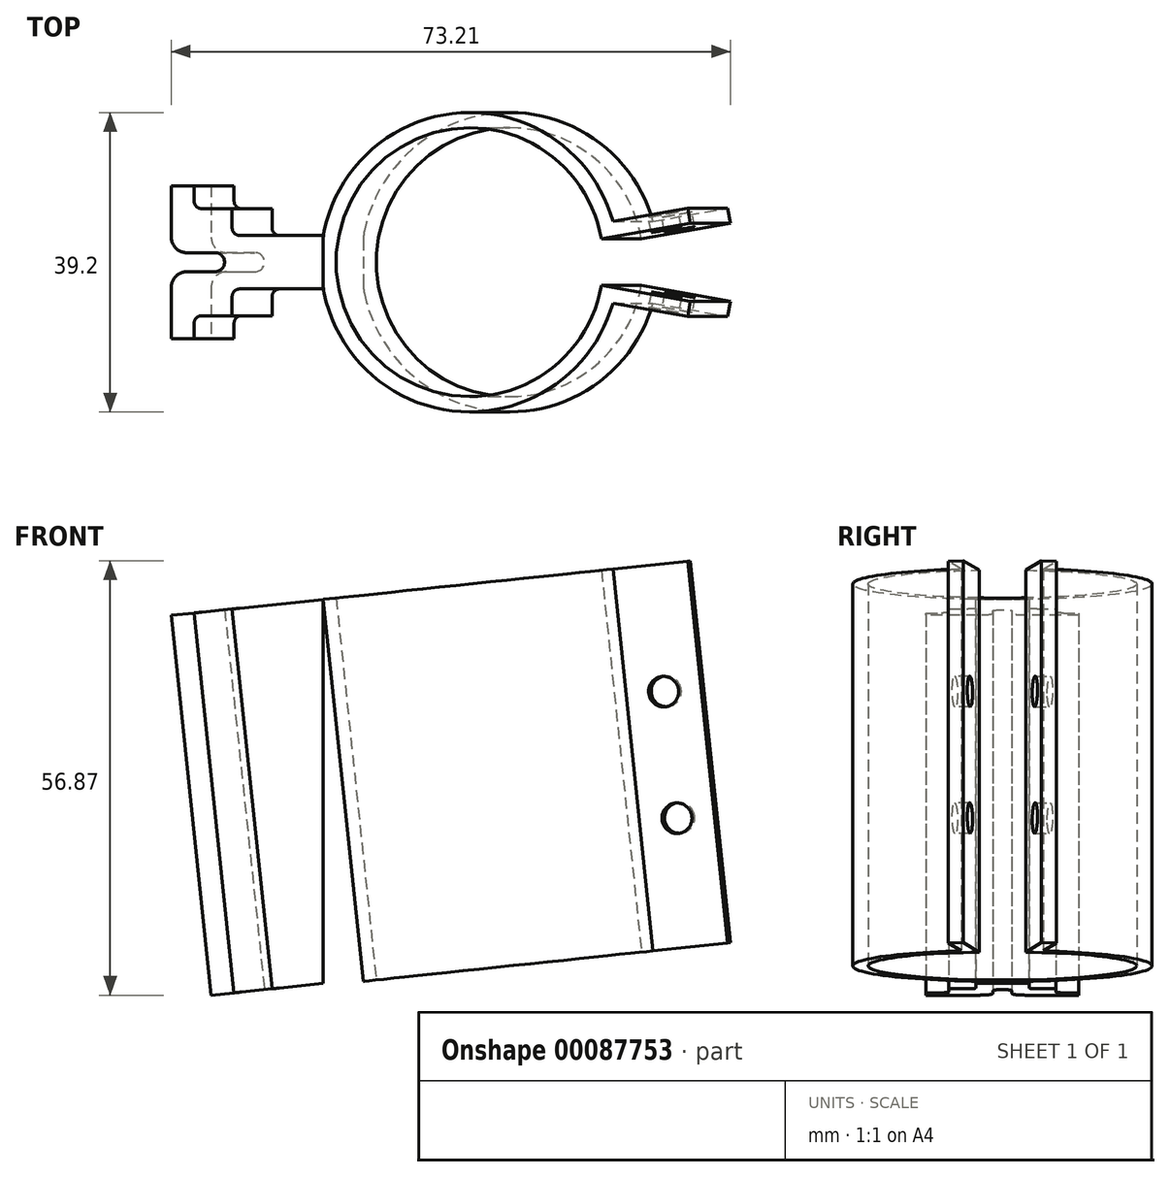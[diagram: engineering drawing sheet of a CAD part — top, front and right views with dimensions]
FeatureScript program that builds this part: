
annotation { "Feature Type Name" : "Feature", "Feature Type Description" : "" }
export const myFeature = defineFeature(function(context is Context, id is Id, definition is map)
    precondition{}
    {
        {
            var Q0;
            Q0=qCreatedBy(makeId("Top.planeOp"),FACE);
            var sketch = newSketch(context, id + "F0", { "sketchPlane" : qUnion([Q0])});
            skCircle(sketch, "E0", {"center": v(0, 0) * mm, "radius": 17.6 * mm});
            skCircle(sketch, "E1", {"center": v(0, 0) * mm, "radius": 19.6 * mm});
            skLineSegment(sketch, "E2", {"start": v(0, 0) * mm, "end": v(44.07, 0) * mm});
            skLineSegment(sketch, "E3", {"start": v(44.07, 0) * mm, "end": v(44.07, 7.77) * mm, "construction": true});
            skLineSegment(sketch, "E4", {"start": v(44.07, 7.77) * mm, "end": v(0, 0) * mm});
            skLineSegment(sketch, "E5.MirrorCS", {"start": v(44.07, -7.77) * mm, "end": v(0, 0) * mm});
            skLineSegment(sketch, "E6", {"start": v(18.85, 5.35) * mm, "end": v(28.7, 7.1) * mm});
            skLineSegment(sketch, "E7", {"start": v(28.7, 7.1) * mm, "end": v(29.05, 5.12) * mm});
            skLineSegment(sketch, "E8", {"start": v(-19.28, 3.5) * mm, "end": v(-31.28, 3.5) * mm});
            skLineSegment(sketch, "E9", {"start": v(-31.28, 3.5) * mm, "end": v(-31.28, 7) * mm});
            skLineSegment(sketch, "E10", {"start": v(-31.28, 7) * mm, "end": v(-36.28, 7) * mm});
            skLineSegment(sketch, "E11", {"start": v(-36.28, -7) * mm, "end": v(-31.28, -7) * mm});
            skLineSegment(sketch, "E12", {"start": v(-31.28, -7) * mm, "end": v(-31.28, -3.5) * mm});
            skLineSegment(sketch, "E13", {"start": v(-31.28, -3.5) * mm, "end": v(-19.28, -3.5) * mm});
            skLineSegment(sketch, "E14", {"start": v(-36.28, 7) * mm, "end": v(-36.28, 10) * mm});
            skLineSegment(sketch, "E15", {"start": v(-36.28, 10) * mm, "end": v(-39.28, 10) * mm});
            skLineSegment(sketch, "E16", {"start": v(-39.28, 10) * mm, "end": v(-39.28, 1.25) * mm});
            skLineSegment(sketch, "E17", {"start": v(-39.28, -1.25) * mm, "end": v(-39.28, -10) * mm});
            skLineSegment(sketch, "E18", {"start": v(-39.28, -10) * mm, "end": v(-36.28, -10) * mm});
            skLineSegment(sketch, "E19", {"start": v(-36.28, -10) * mm, "end": v(-36.28, -7) * mm});
            skLineSegment(sketch, "E20.MirrorCS", {"start": v(18.85, -5.35) * mm, "end": v(28.7, -7.1) * mm});
            skLineSegment(sketch, "E21.MirrorCS", {"start": v(28.7, -7.1) * mm, "end": v(29.05, -5.12) * mm});
            skLineSegment(sketch, "E22", {"start": v(-39.28, -1.25) * mm, "end": v(-33.53, -1.25) * mm});
            skLineSegment(sketch, "E23", {"start": v(-33.53, 1.25) * mm, "end": v(-39.28, 1.25) * mm});
            skArc(sketch, "E24", {"start": v(-33.53, -1.25) * mm, "mid": v(-32.28, 0) * mm, "end": v(-33.53, 1.25) * mm});
            skLineSegment(sketch, "E25", {"start": v(-32.28, 0) * mm, "end": v(-32.28, -10.85) * mm, "construction": true});
            skSolve(sketch);
        }
        {
            var Q0;
            {var subQ1=sQuery(id+"F0.wireOp",EDGE,"E8");Q0=makeQuery(id+"F0.imprint","IMPRINT",FACE,{"disambiguationData":[TD([[makeQuery(id+"F0.imprint","IMPRINT",EDGE,{"derivedFrom":subQ1}),1.0]])]});}
            var Q1;
            {var subQ3=sQuery(id+"F0.wireOp",EDGE,"E4");var subQ5=sQuery(id+"F0.wireOp",EDGE,"E0");var subQ6=makeQuery(id+"F0.imprint","INTERSECT",VERTEX,{"derivedFrom":[subQ5,subQ3]});Q1=makeQuery(id+"F0.imprint","IMPRINT",FACE,{"disambiguationData":[TD([[makeQuery(id+"F0.imprint","IMPRINT",EDGE,{"disambiguationData":[TD([[subQ6,-1.0]])],"derivedFrom":subQ5}),-1.0]])]});}
            var Q2;
            {var subQ0=sQuery(id+"F0.wireOp",EDGE,"E6");Q2=makeQuery(id+"F0.imprint","IMPRINT",FACE,{"disambiguationData":[TD([[makeQuery(id+"F0.imprint","IMPRINT",EDGE,{"derivedFrom":subQ0}),-1.0]])]});}
            var Q3;
            {var subQ0=sQuery(id+"F0.wireOp",EDGE,"E20.MirrorCS");Q3=makeQuery(id+"F0.imprint","IMPRINT",FACE,{"disambiguationData":[TD([[makeQuery(id+"F0.imprint","IMPRINT",EDGE,{"derivedFrom":subQ0}),1.0]])]});}
            extrude(context, id + "F1", {"entities" : qUnion([Q0, Q1, Q2, Q3]), "depth" : 50 * mm});
        }
        {
            var Q0;
            Q0=makeQuery(id+"F1.opExtrude","SWEPT_EDGE",EDGE,{"disambiguationData":[OSD([sQuery(id+"F0.wireOp",EDGE,"E12"),sQuery(id+"F0.wireOp",EDGE,"E13")])]});
            var Q1;
            Q1=makeQuery(id+"F1.opExtrude","SWEPT_EDGE",EDGE,{"disambiguationData":[OSD([sQuery(id+"F0.wireOp",EDGE,"E11"),sQuery(id+"F0.wireOp",EDGE,"E19")])]});
            var Q2;
            Q2=makeQuery(id+"F1.opExtrude","SWEPT_EDGE",EDGE,{"disambiguationData":[OSD([sQuery(id+"F0.wireOp",EDGE,"E8"),sQuery(id+"F0.wireOp",EDGE,"E9")])]});
            var Q3;
            Q3=makeQuery(id+"F1.opExtrude","SWEPT_EDGE",EDGE,{"disambiguationData":[OSD([sQuery(id+"F0.wireOp",EDGE,"E10"),sQuery(id+"F0.wireOp",EDGE,"E14")])]});
            fillet(context, id + "F2", {"entities" : qUnion([Q0, Q1, Q2, Q3]), "radius" : 1 * mm, "tangentPropagation" : true, "allowEdgeOverflow" : false});
        }
        {
            var Q0;
            Q0=makeQuery(id+"F1.opExtrude","SWEPT_FACE",FACE,{"disambiguationData":[OSD([sQuery(id+"F0.wireOp",EDGE,"E20.MirrorCS")])]});
            var sketch = newSketch(context, id + "F3", { "sketchPlane" : qUnion([Q0])});
            skLineSegment(sketch, "E26.bottom", {"start": v(19.5, 50) * mm, "end": v(29.5, 50) * mm, "construction": true});
            skLineSegment(sketch, "E26.top", {"start": v(19.5, 0) * mm, "end": v(29.5, 0) * mm, "construction": true});
            skLineSegment(sketch, "E26.left", {"start": v(19.5, 50) * mm, "end": v(19.5, 0) * mm, "construction": true});
            skLineSegment(sketch, "E26.right", {"start": v(29.5, 50) * mm, "end": v(29.5, 0) * mm, "construction": true});
            skLineSegment(sketch, "E27", {"start": v(24.5, 50) * mm, "end": v(24.5, 33.33) * mm, "construction": true});
            skLineSegment(sketch, "E28", {"start": v(24.5, 33.33) * mm, "end": v(24.5, 16.67) * mm, "construction": true});
            skLineSegment(sketch, "E29", {"start": v(24.5, 16.67) * mm, "end": v(24.5, 0) * mm, "construction": true});
            skCircle(sketch, "E30", {"center": v(24.5, 33.33) * mm, "radius": 2 * mm});
            skCircle(sketch, "E31", {"center": v(24.5, 16.67) * mm, "radius": 2 * mm});
            skSolve(sketch);
        }
        {
            var Q0;
            Q0 = qSketchRegion(id + "F3", true);
            extrude(context, id + "F4", {"entities" : qUnion([Q0]), "operationType" : NewBodyOperationType.REMOVE, "oppositeDirection" : true, "depth" : 5 * mm});
        }
        {
            var Q0;
            Q0=makeQuery(id+"F1.opExtrude","SWEPT_FACE",FACE,{"disambiguationData":[OSD([sQuery(id+"F0.wireOp",EDGE,"E6")])]});
            var sketch = newSketch(context, id + "F5", { "sketchPlane" : qUnion([Q0])});
            skLineSegment(sketch, "E32.bottom", {"start": v(-29.5, 50) * mm, "end": v(-19.5, 50) * mm, "construction": true});
            skLineSegment(sketch, "E32.top", {"start": v(-29.5, 0) * mm, "end": v(-19.5, 0) * mm, "construction": true});
            skLineSegment(sketch, "E32.left", {"start": v(-29.5, 50) * mm, "end": v(-29.5, 0) * mm, "construction": true});
            skLineSegment(sketch, "E32.right", {"start": v(-19.5, 50) * mm, "end": v(-19.5, 0) * mm, "construction": true});
            skLineSegment(sketch, "E33", {"start": v(-24.5, 50) * mm, "end": v(-24.5, 33.33) * mm, "construction": true});
            skLineSegment(sketch, "E34", {"start": v(-24.5, 33.33) * mm, "end": v(-24.5, 16.67) * mm, "construction": true});
            skLineSegment(sketch, "E35", {"start": v(-24.5, 16.67) * mm, "end": v(-24.5, 0) * mm, "construction": true});
            skCircle(sketch, "E36", {"center": v(-24.5, 33.33) * mm, "radius": 2 * mm});
            skCircle(sketch, "E37", {"center": v(-24.5, 16.67) * mm, "radius": 2 * mm});
            skSolve(sketch);
        }
        {
            var Q0;
            Q0 = qSketchRegion(id + "F5", true);
            extrude(context, id + "F6", {"entities" : qUnion([Q0]), "operationType" : NewBodyOperationType.REMOVE, "oppositeDirection" : true, "depth" : 5 * mm});
        }
        {
            var Q0;
            Q0=makeQuery(id+"F1.opExtrude","SWEPT_EDGE",EDGE,{"disambiguationData":[OSD([sQuery(id+"F0.wireOp",EDGE,"E16"),sQuery(id+"F0.wireOp",EDGE,"E23")])]});
            var Q1;
            Q1=makeQuery(id+"F1.opExtrude","SWEPT_EDGE",EDGE,{"disambiguationData":[OSD([sQuery(id+"F0.wireOp",EDGE,"E17"),sQuery(id+"F0.wireOp",EDGE,"E22")])]});
            fillet(context, id + "F7", {"entities" : qUnion([Q0, Q1]), "radius" : 2 * mm, "tangentPropagation" : true, "allowEdgeOverflow" : false});
        }
        {
            var Q0;
            Q0=makeQuery(id+"F1.opExtrude","SWEPT_FACE",FACE,{"disambiguationData":[OSD([sQuery(id+"F0.wireOp",EDGE,"E13")])]});
            var sketch = newSketch(context, id + "F8", { "sketchPlane" : qUnion([Q0])});
            skLineSegment(sketch, "E38", {"start": v(-19.28, 50) * mm, "end": v(-19.28, 0) * mm});
            skLineSegment(sketch, "E39", {"start": v(-19.28, 0) * mm, "end": v(-24.54, 0) * mm});
            skLineSegment(sketch, "E40", {"start": v(-24.54, 0) * mm, "end": v(-19.28, 50) * mm});
            skSolve(sketch);
        }
        {
            var Q0;
            Q0=makeQuery(id+"F8.imprint","IMPRINT",FACE,{"disambiguationData":[TD([[makeQuery(id+"F8.imprint","IMPRINT",EDGE,{"derivedFrom":sQuery(id+"F8.wireOp",EDGE,"E38")}),-1.0]])]});
            extrude(context, id + "F9", {"entities" : qUnion([Q0]), "operationType" : NewBodyOperationType.REMOVE, "oppositeDirection" : true, "depth" : 25 * mm});
        }
        {
            var Q0;
            Q0=makeQuery(id+"F9.boolean.opBoolean","SPLIT",BODY,{"disambiguationData":[OD(1.0)],"derivedFrom":makeQuery(id+"F1.opExtrude","SWEPT_BODY",BODY,{"disambiguationData":[OSD([sQuery(id+"F0.wireOp",EDGE,"E0"),sQuery(id+"F0.wireOp",EDGE,"E1"),sQuery(id+"F0.wireOp",EDGE,"E4"),sQuery(id+"F0.wireOp",EDGE,"E5.MirrorCS"),sQuery(id+"F0.wireOp",EDGE,"E6"),sQuery(id+"F0.wireOp",EDGE,"E7"),sQuery(id+"F0.wireOp",EDGE,"E8"),sQuery(id+"F0.wireOp",EDGE,"E9"),sQuery(id+"F0.wireOp",EDGE,"E10"),sQuery(id+"F0.wireOp",EDGE,"E11"),sQuery(id+"F0.wireOp",EDGE,"E12"),sQuery(id+"F0.wireOp",EDGE,"E13"),sQuery(id+"F0.wireOp",EDGE,"E14"),sQuery(id+"F0.wireOp",EDGE,"E15"),sQuery(id+"F0.wireOp",EDGE,"E16"),sQuery(id+"F0.wireOp",EDGE,"E17"),sQuery(id+"F0.wireOp",EDGE,"E18"),sQuery(id+"F0.wireOp",EDGE,"E19"),sQuery(id+"F0.wireOp",EDGE,"E20.MirrorCS"),sQuery(id+"F0.wireOp",EDGE,"E21.MirrorCS"),sQuery(id+"F0.wireOp",EDGE,"E22"),sQuery(id+"F0.wireOp",EDGE,"E23"),sQuery(id+"F0.wireOp",EDGE,"E24")])]})});
            var Q1;
            {var subQ1=sQuery(id+"F0.wireOp",EDGE,"E13");var subQ5=sQuery(id+"F8.wireOp",EDGE,"E38");Q1=makeQuery(id+"F9.boolean.opBoolean","COPY",EDGE,{"disambiguationData":[TD([makeQuery(id+"F9.opExtrude","SWEPT_FACE",FACE,{"disambiguationData":[OSD([subQ5])]})])],"derivedFrom":makeQuery(id+"F9.opExtrude","SWEPT_EDGE",EDGE,{"disambiguationData":[OSD([subQ1,subQ5,sQuery(id+"F8.wireOp",EDGE,"E40")])]})});}
            transform(context, id + "F10", {"entities" : qUnion([Q0]), "transformType" : TransformType.ROTATION, "transformAxis" : qUnion([Q1]), "angle" : 6 * degree, "makeCopy" : false});
        }
        {
            var Q0;
            Q0=makeQuery(id+"F9.boolean.opBoolean","SPLIT",BODY,{"disambiguationData":[OD(1.0)],"derivedFrom":makeQuery(id+"F1.opExtrude","SWEPT_BODY",BODY,{"disambiguationData":[OSD([sQuery(id+"F0.wireOp",EDGE,"E0"),sQuery(id+"F0.wireOp",EDGE,"E1"),sQuery(id+"F0.wireOp",EDGE,"E4"),sQuery(id+"F0.wireOp",EDGE,"E5.MirrorCS"),sQuery(id+"F0.wireOp",EDGE,"E6"),sQuery(id+"F0.wireOp",EDGE,"E7"),sQuery(id+"F0.wireOp",EDGE,"E8"),sQuery(id+"F0.wireOp",EDGE,"E9"),sQuery(id+"F0.wireOp",EDGE,"E10"),sQuery(id+"F0.wireOp",EDGE,"E11"),sQuery(id+"F0.wireOp",EDGE,"E12"),sQuery(id+"F0.wireOp",EDGE,"E13"),sQuery(id+"F0.wireOp",EDGE,"E14"),sQuery(id+"F0.wireOp",EDGE,"E15"),sQuery(id+"F0.wireOp",EDGE,"E16"),sQuery(id+"F0.wireOp",EDGE,"E17"),sQuery(id+"F0.wireOp",EDGE,"E18"),sQuery(id+"F0.wireOp",EDGE,"E19"),sQuery(id+"F0.wireOp",EDGE,"E20.MirrorCS"),sQuery(id+"F0.wireOp",EDGE,"E21.MirrorCS"),sQuery(id+"F0.wireOp",EDGE,"E22"),sQuery(id+"F0.wireOp",EDGE,"E23"),sQuery(id+"F0.wireOp",EDGE,"E24")])]})});
            var Q1;
            Q1=makeQuery(id+"F9.boolean.opBoolean","SPLIT",BODY,{"disambiguationData":[OD(0.0)],"derivedFrom":makeQuery(id+"F1.opExtrude","SWEPT_BODY",BODY,{"disambiguationData":[OSD([sQuery(id+"F0.wireOp",EDGE,"E0"),sQuery(id+"F0.wireOp",EDGE,"E1"),sQuery(id+"F0.wireOp",EDGE,"E4"),sQuery(id+"F0.wireOp",EDGE,"E5.MirrorCS"),sQuery(id+"F0.wireOp",EDGE,"E6"),sQuery(id+"F0.wireOp",EDGE,"E7"),sQuery(id+"F0.wireOp",EDGE,"E8"),sQuery(id+"F0.wireOp",EDGE,"E9"),sQuery(id+"F0.wireOp",EDGE,"E10"),sQuery(id+"F0.wireOp",EDGE,"E11"),sQuery(id+"F0.wireOp",EDGE,"E12"),sQuery(id+"F0.wireOp",EDGE,"E13"),sQuery(id+"F0.wireOp",EDGE,"E14"),sQuery(id+"F0.wireOp",EDGE,"E15"),sQuery(id+"F0.wireOp",EDGE,"E16"),sQuery(id+"F0.wireOp",EDGE,"E17"),sQuery(id+"F0.wireOp",EDGE,"E18"),sQuery(id+"F0.wireOp",EDGE,"E19"),sQuery(id+"F0.wireOp",EDGE,"E20.MirrorCS"),sQuery(id+"F0.wireOp",EDGE,"E21.MirrorCS"),sQuery(id+"F0.wireOp",EDGE,"E22"),sQuery(id+"F0.wireOp",EDGE,"E23"),sQuery(id+"F0.wireOp",EDGE,"E24")])]})});
            booleanBodies(context, id + "F11", {"operationType" : BooleanOperationType.UNION, "tools" : qUnion([Q0, Q1])});
        }
        {
            var Q0;
            {var subQ0=sQuery(id+"F0.wireOp",EDGE,"E4");var subQ1=sQuery(id+"F0.wireOp",EDGE,"E13");var subQ2=sQuery(id+"F0.wireOp",EDGE,"E1");var subQ3=sQuery(id+"F0.wireOp",EDGE,"E20.MirrorCS");var subQ4=sQuery(id+"F0.wireOp",EDGE,"E6");var subQ5=sQuery(id+"F0.wireOp",EDGE,"E8");var subQ6=sQuery(id+"F0.wireOp",EDGE,"E21.MirrorCS");var subQ7=sQuery(id+"F0.wireOp",EDGE,"E0");var subQ8=sQuery(id+"F0.wireOp",EDGE,"E5.MirrorCS");var subQ9=sQuery(id+"F0.wireOp",EDGE,"E7");Q0=makeQuery(id+"F9.boolean.opBoolean","SPLIT",FACE,{"disambiguationData":[TD([makeQuery(id+"F1.opExtrude","SWEPT_FACE",FACE,{"disambiguationData":[OSD([subQ7])]})])],"derivedFrom":makeQuery(id+"F1.opExtrude","CAP_FACE",FACE,{"disambiguationData":[OSD([subQ7,subQ2,subQ0,subQ8,subQ4,subQ9,subQ5,sQuery(id+"F0.wireOp",EDGE,"E9"),sQuery(id+"F0.wireOp",EDGE,"E10"),sQuery(id+"F0.wireOp",EDGE,"E11"),sQuery(id+"F0.wireOp",EDGE,"E12"),subQ1,sQuery(id+"F0.wireOp",EDGE,"E14"),sQuery(id+"F0.wireOp",EDGE,"E15"),sQuery(id+"F0.wireOp",EDGE,"E16"),sQuery(id+"F0.wireOp",EDGE,"E17"),sQuery(id+"F0.wireOp",EDGE,"E18"),sQuery(id+"F0.wireOp",EDGE,"E19"),subQ3,subQ6,sQuery(id+"F0.wireOp",EDGE,"E22"),sQuery(id+"F0.wireOp",EDGE,"E23"),sQuery(id+"F0.wireOp",EDGE,"E24")])],"isStart":true})});}
            extrude(context, id + "F12", {"entities" : qUnion([Q0]), "operationType" : NewBodyOperationType.ADD, "depth" : 0.28 * mm});
        }
        {
            var Q0;
            {var subQ0=sQuery(id+"F0.wireOp",EDGE,"E8");var subQ1=sQuery(id+"F0.wireOp",EDGE,"E1");var subQ2=makeQuery(id+"F9.boolean.opBoolean","INTERSECT",EDGE,{"derivedFrom":[makeQuery(id+"F1.opExtrude","SWEPT_FACE",FACE,{"disambiguationData":[OSD([subQ0])]}),makeQuery(id+"F9.opExtrude","SWEPT_FACE",FACE,{"disambiguationData":[OSD([sQuery(id+"F8.wireOp",EDGE,"E40")])]})]});Q0=makeQuery(id+"F12.boolean.opBoolean","MERGE",EDGE,{"derivedFrom":[makeQuery(id+"F11.opBoolean","MERGE",EDGE,{"derivedFrom":[subQ2,makeQuery(id+"F1.opExtrude","SWEPT_EDGE",EDGE,{"disambiguationData":[OSD([subQ1,subQ0])]})]}),makeQuery(id+"F11.opBoolean","SPLIT",EDGE,{"derivedFrom":subQ2}),makeQuery(id+"F12.opExtrude","SWEPT_EDGE",EDGE,{"disambiguationData":[OSD([subQ1,subQ0])]})]});}
            var Q1;
            {var subQ0=sQuery(id+"F8.wireOp",EDGE,"E38");var subQ1=sQuery(id+"F0.wireOp",EDGE,"E13");var subQ2=sQuery(id+"F0.wireOp",EDGE,"E1");var subQ3=makeQuery(id+"F9.boolean.opBoolean","COPY",EDGE,{"derivedFrom":makeQuery(id+"F9.opExtrude","CAP_EDGE",EDGE,{"disambiguationData":[OSD([sQuery(id+"F8.wireOp",EDGE,"E40")])],"isStart":true})});Q1=makeQuery(id+"F12.boolean.opBoolean","MERGE",EDGE,{"derivedFrom":[makeQuery(id+"F11.opBoolean","MERGE",EDGE,{"derivedFrom":[makeQuery(id+"F9.boolean.opBoolean","MERGE",EDGE,{"derivedFrom":[makeQuery(id+"F1.opExtrude","SWEPT_EDGE",EDGE,{"disambiguationData":[OSD([subQ2,subQ1])]}),makeQuery(id+"F9.opExtrude","CAP_EDGE",EDGE,{"disambiguationData":[OSD([subQ0])],"isStart":true})]}),subQ3]}),makeQuery(id+"F11.opBoolean","SPLIT",EDGE,{"derivedFrom":subQ3}),makeQuery(id+"F12.opExtrude","SWEPT_EDGE",EDGE,{"disambiguationData":[OSD([subQ2,subQ1,subQ0,sQuery(id+"F8.wireOp",EDGE,"E39")])]})]});}
            fillet(context, id + "F13", {"entities" : qUnion([Q0, Q1]), "radius" : 5 * mm, "tangentPropagation" : true, "allowEdgeOverflow" : false});
        }
    });
